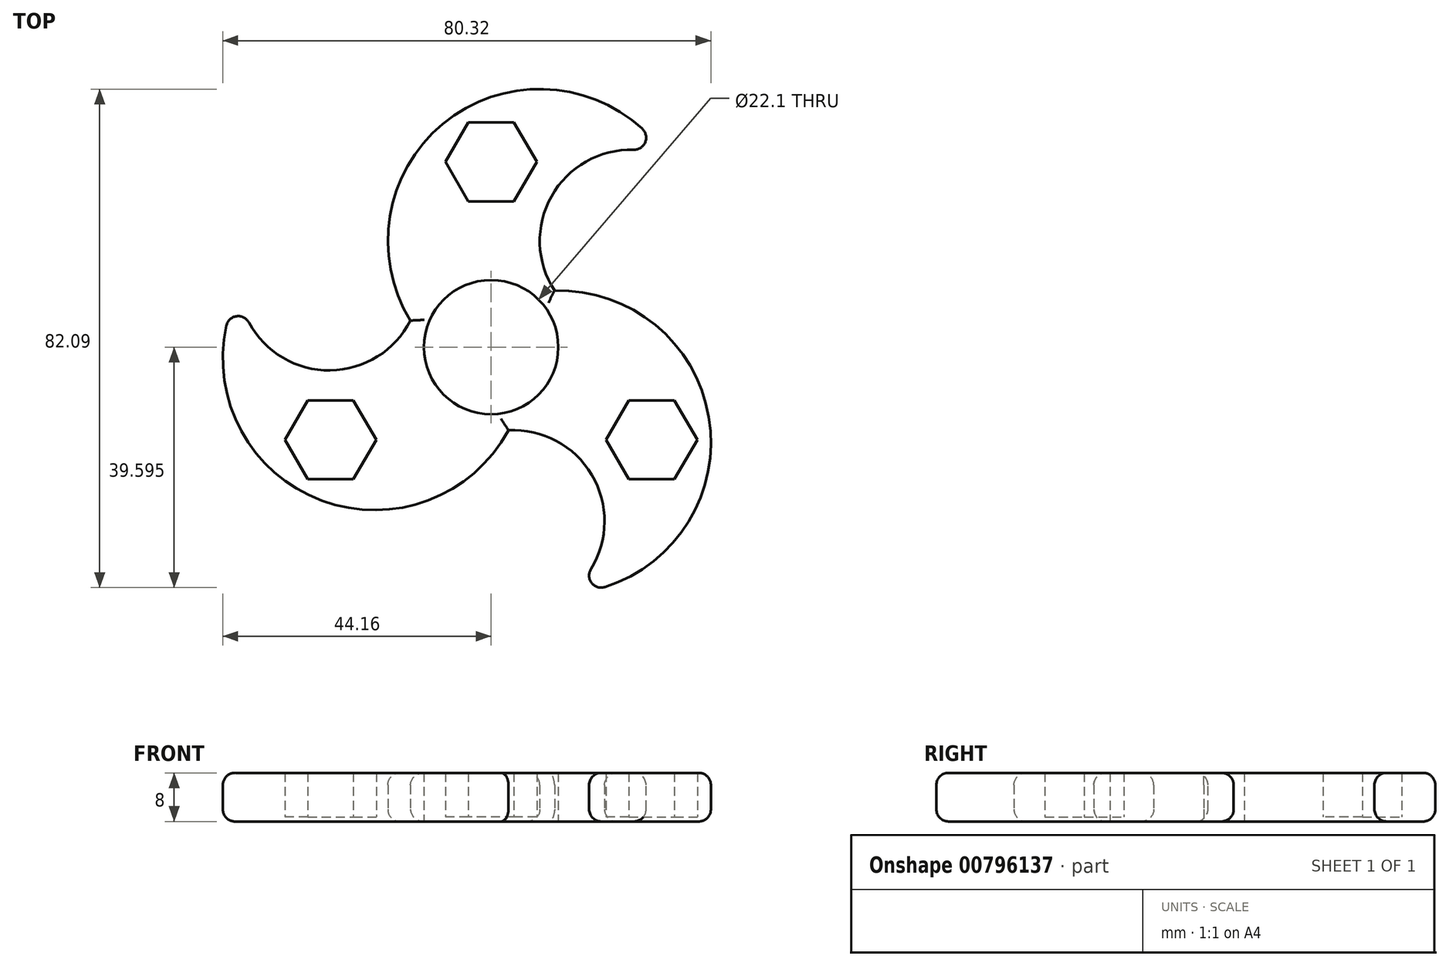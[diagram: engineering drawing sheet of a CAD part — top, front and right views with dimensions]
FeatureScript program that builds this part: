
annotation { "Feature Type Name" : "Feature", "Feature Type Description" : "" }
export const myFeature = defineFeature(function(context is Context, id is Id, definition is map)
    precondition{}
    {
        {
            var Q0;
            Q0=qCreatedBy(makeId("Top.planeOp"),FACE);
            var sketch = newSketch(context, id + "F0", { "sketchPlane" : qUnion([Q0])});
            skCircle(sketch, "E0", {"center": v(0, -1.85) * mm, "radius": 11.05 * mm});
            skLineSegment(sketch, "E1", {"start": v(0, -1.85) * mm, "end": v(0, 49.7) * mm, "construction": true});
            skLineSegment(sketch, "E2", {"start": v(0, -1.85) * mm, "end": v(-44.64, -27.62) * mm, "construction": true});
            skLineSegment(sketch, "E3", {"start": v(0, -1.85) * mm, "end": v(44.64, -27.62) * mm, "construction": true});
            skCircle(sketch, "E4", {"center": v(0, -1.85) * mm, "radius": 30.5 * mm, "construction": true});
            skPoint(sketch, "E5", {"position": v(-26.41, -17.1) * mm});
            skPoint(sketch, "E6", {"position": v(26.41, -17.1) * mm});
            skPoint(sketch, "E7", {"position": v(0, 28.65) * mm});
            skCircle(sketch, "E8", {"center": v(0, -1.85) * mm, "radius": 17.5 * mm, "construction": true});
            skPoint(sketch, "E9", {"position": v(0, 15.65) * mm});
            skPoint(sketch, "E10", {"position": v(15.16, -10.6) * mm});
            skPoint(sketch, "E11", {"position": v(-15.16, -10.6) * mm});
            skLineSegment(sketch, "E12", {"start": v(-15.16, -10.6) * mm, "end": v(-23.16, 3.26) * mm, "construction": true});
            skLineSegment(sketch, "E13", {"start": v(-15.16, -10.6) * mm, "end": v(-7.16, -24.45) * mm, "construction": true});
            skLineSegment(sketch, "E14", {"start": v(15.16, -10.6) * mm, "end": v(7.16, -24.45) * mm, "construction": true});
            skLineSegment(sketch, "E15", {"start": v(15.16, -10.6) * mm, "end": v(23.16, 3.26) * mm, "construction": true});
            skLineSegment(sketch, "E16", {"start": v(0, 15.65) * mm, "end": v(16, 15.65) * mm, "construction": true});
            skLineSegment(sketch, "E17", {"start": v(0, 15.65) * mm, "end": v(-16, 15.65) * mm, "construction": true});
            skPoint(sketch, "E18", {"position": v(-19.16, -3.67) * mm});
            skPoint(sketch, "E19", {"position": v(-11.16, -17.52) * mm});
            skPoint(sketch, "E20", {"position": v(-8, 15.65) * mm});
            skPoint(sketch, "E21", {"position": v(8, 15.65) * mm});
            skPoint(sketch, "E22", {"position": v(19.16, -3.67) * mm});
            skPoint(sketch, "E23", {"position": v(11.16, -17.52) * mm});
            skCircle(sketch, "E24", {"center": v(0, -1.85) * mm, "radius": 14 * mm});
            skCircle(sketch, "E25", {"center": v(8, 15.65) * mm, "radius": 25 * mm});
            skCircle(sketch, "E26", {"center": v(11.16, -17.52) * mm, "radius": 25 * mm});
            skCircle(sketch, "E27", {"center": v(-19.16, -3.67) * mm, "radius": 25 * mm});
            skCircle(sketch, "E28.cCircle", {"center": v(0, 28.65) * mm, "radius": 6.5 * mm, "construction": true});
            skLineSegment(sketch, "E28.0", {"start": v(3.75, 22.15) * mm, "end": v(-3.75, 22.15) * mm});
            skLineSegment(sketch, "E28.1", {"start": v(-3.75, 22.15) * mm, "end": v(-7.5, 28.65) * mm});
            skLineSegment(sketch, "E28.2", {"start": v(-7.5, 28.65) * mm, "end": v(-3.75, 35.15) * mm});
            skLineSegment(sketch, "E28.3", {"start": v(-3.75, 35.15) * mm, "end": v(3.75, 35.15) * mm});
            skLineSegment(sketch, "E28.4", {"start": v(3.75, 35.15) * mm, "end": v(7.5, 28.65) * mm});
            skLineSegment(sketch, "E28.5", {"start": v(7.5, 28.65) * mm, "end": v(3.75, 22.15) * mm});
            skPoint(sketch, "E28.0.midPoint", {"position": v(0, 22.15) * mm});
            skCircle(sketch, "E29.cCircle", {"center": v(26.41, -17.1) * mm, "radius": 6.5 * mm, "construction": true});
            skLineSegment(sketch, "E29.0", {"start": v(18.9, -17.1) * mm, "end": v(22.66, -10.6) * mm});
            skLineSegment(sketch, "E29.1", {"start": v(22.66, -10.6) * mm, "end": v(30.17, -10.6) * mm});
            skLineSegment(sketch, "E29.2", {"start": v(30.17, -10.6) * mm, "end": v(33.92, -17.1) * mm});
            skLineSegment(sketch, "E29.3", {"start": v(33.92, -17.1) * mm, "end": v(30.17, -23.6) * mm});
            skLineSegment(sketch, "E29.4", {"start": v(30.17, -23.6) * mm, "end": v(22.66, -23.6) * mm});
            skLineSegment(sketch, "E29.5", {"start": v(22.66, -23.6) * mm, "end": v(18.9, -17.1) * mm});
            skPoint(sketch, "E29.0.midPoint", {"position": v(20.78, -13.85) * mm});
            skCircle(sketch, "E30.cCircle", {"center": v(-26.41, -17.1) * mm, "radius": 6.5 * mm, "construction": true});
            skLineSegment(sketch, "E30.0", {"start": v(-22.66, -10.6) * mm, "end": v(-18.9, -17.1) * mm});
            skLineSegment(sketch, "E30.1", {"start": v(-18.9, -17.1) * mm, "end": v(-22.66, -23.6) * mm});
            skLineSegment(sketch, "E30.2", {"start": v(-22.66, -23.6) * mm, "end": v(-30.17, -23.6) * mm});
            skLineSegment(sketch, "E30.3", {"start": v(-30.17, -23.6) * mm, "end": v(-33.92, -17.1) * mm});
            skLineSegment(sketch, "E30.4", {"start": v(-33.92, -17.1) * mm, "end": v(-30.17, -10.6) * mm});
            skLineSegment(sketch, "E30.5", {"start": v(-30.17, -10.6) * mm, "end": v(-22.66, -10.6) * mm});
            skPoint(sketch, "E30.0.midPoint", {"position": v(-20.78, -13.85) * mm});
            skPoint(sketch, "E31", {"position": v(23, 15.65) * mm});
            skPoint(sketch, "E32", {"position": v(-26.66, 9.32) * mm});
            skPoint(sketch, "E33", {"position": v(3.66, -30.51) * mm});
            skCircle(sketch, "E34", {"center": v(23, 15.65) * mm, "radius": 15 * mm});
            skCircle(sketch, "E35", {"center": v(3.66, -30.51) * mm, "radius": 15 * mm});
            skCircle(sketch, "E36", {"center": v(-26.66, 9.32) * mm, "radius": 15 * mm});
            skSolve(sketch);
        }
        {
            var Q0;
            Q0=makeQuery(id+"F0.imprint","IMPRINT",FACE,{"disambiguationData":[TD([[makeQuery(id+"F0.imprint","IMPRINT",EDGE,{"derivedFrom":sQuery(id+"F0.wireOp",EDGE,"E30.0")}),1.0]])]});
            var Q1;
            Q1=makeQuery(id+"F0.imprint","IMPRINT",FACE,{"disambiguationData":[TD([[makeQuery(id+"F0.imprint","IMPRINT",EDGE,{"derivedFrom":sQuery(id+"F0.wireOp",EDGE,"E28.0")}),1.0]])]});
            var Q2;
            Q2=makeQuery(id+"F0.imprint","IMPRINT",FACE,{"disambiguationData":[TD([[makeQuery(id+"F0.imprint","IMPRINT",EDGE,{"derivedFrom":sQuery(id+"F0.wireOp",EDGE,"E29.0")}),1.0]])]});
            var Q3;
            {var subQ1=sQuery(id+"F0.wireOp",EDGE,"E0");var subQ5=sQuery(id+"F0.wireOp",EDGE,"E25");var subQ6=makeQuery(id+"F0.imprint","INTERSECT",VERTEX,{"disambiguationData":[OD(0.0)],"derivedFrom":[subQ1,subQ5]});Q3=makeQuery(id+"F0.imprint","IMPRINT",FACE,{"disambiguationData":[TD([[makeQuery(id+"F0.imprint","IMPRINT",EDGE,{"disambiguationData":[TD([[subQ6,-1.0]])],"derivedFrom":subQ1}),-1.0]])]});}
            var Q4;
            {var subQ0=sQuery(id+"F0.wireOp",EDGE,"E27");var subQ1=sQuery(id+"F0.wireOp",EDGE,"E0");var subQ2=makeQuery(id+"F0.imprint","INTERSECT",VERTEX,{"disambiguationData":[OD(0.0)],"derivedFrom":[subQ1,subQ0]});Q4=makeQuery(id+"F0.imprint","IMPRINT",FACE,{"disambiguationData":[TD([[makeQuery(id+"F0.imprint","IMPRINT",EDGE,{"disambiguationData":[TD([[subQ2,-1.0]])],"derivedFrom":subQ1}),-1.0]])]});}
            var Q5;
            {var subQ0=sQuery(id+"F0.wireOp",EDGE,"E27");var subQ1=sQuery(id+"F0.wireOp",EDGE,"E0");var subQ2=makeQuery(id+"F0.imprint","INTERSECT",VERTEX,{"disambiguationData":[OD(0.0)],"derivedFrom":[subQ1,subQ0]});Q5=makeQuery(id+"F0.imprint","IMPRINT",FACE,{"disambiguationData":[TD([[makeQuery(id+"F0.imprint","IMPRINT",EDGE,{"disambiguationData":[TD([[subQ2,1.0]])],"derivedFrom":subQ1}),-1.0]])]});}
            var Q6;
            {var subQ0=sQuery(id+"F0.wireOp",EDGE,"E26");var subQ1=sQuery(id+"F0.wireOp",EDGE,"E0");var subQ2=makeQuery(id+"F0.imprint","INTERSECT",VERTEX,{"disambiguationData":[OD(0.0)],"derivedFrom":[subQ1,subQ0]});Q6=makeQuery(id+"F0.imprint","IMPRINT",FACE,{"disambiguationData":[TD([[makeQuery(id+"F0.imprint","IMPRINT",EDGE,{"disambiguationData":[TD([[subQ2,1.0]])],"derivedFrom":subQ1}),-1.0]])]});}
            var Q7;
            {var subQ0=sQuery(id+"F0.wireOp",EDGE,"E27");var subQ1=sQuery(id+"F0.wireOp",EDGE,"E0");var subQ2=makeQuery(id+"F0.imprint","INTERSECT",VERTEX,{"disambiguationData":[OD(1.0)],"derivedFrom":[subQ1,subQ0]});Q7=makeQuery(id+"F0.imprint","IMPRINT",FACE,{"disambiguationData":[TD([[makeQuery(id+"F0.imprint","IMPRINT",EDGE,{"disambiguationData":[TD([[subQ2,-1.0]])],"derivedFrom":subQ1}),-1.0]])]});}
            var Q8;
            {var subQ1=sQuery(id+"F0.wireOp",EDGE,"E0");var subQ5=sQuery(id+"F0.wireOp",EDGE,"E26");var subQ6=makeQuery(id+"F0.imprint","INTERSECT",VERTEX,{"disambiguationData":[OD(1.0)],"derivedFrom":[subQ1,subQ5]});Q8=makeQuery(id+"F0.imprint","IMPRINT",FACE,{"disambiguationData":[TD([[makeQuery(id+"F0.imprint","IMPRINT",EDGE,{"disambiguationData":[TD([[subQ6,-1.0]])],"derivedFrom":subQ1}),-1.0]])]});}
            var Q9;
            {var subQ0=sQuery(id+"F0.wireOp",EDGE,"E36");var subQ1=sQuery(id+"F0.wireOp",EDGE,"E24");var subQ2=makeQuery(id+"F0.imprint","INTERSECT",VERTEX,{"disambiguationData":[OD(0.0)],"derivedFrom":[subQ1,subQ0]});Q9=makeQuery(id+"F0.imprint","IMPRINT",FACE,{"disambiguationData":[TD([[makeQuery(id+"F0.imprint","IMPRINT",EDGE,{"disambiguationData":[TD([[subQ2,-1.0]])],"derivedFrom":subQ1}),-1.0]])]});}
            var Q10;
            {var subQ0=sQuery(id+"F0.wireOp",EDGE,"E27");var subQ1=sQuery(id+"F0.wireOp",EDGE,"E24");var subQ2=makeQuery(id+"F0.imprint","INTERSECT",VERTEX,{"disambiguationData":[OD(0.0)],"derivedFrom":[subQ1,subQ0]});Q10=makeQuery(id+"F0.imprint","IMPRINT",FACE,{"disambiguationData":[TD([[makeQuery(id+"F0.imprint","IMPRINT",EDGE,{"disambiguationData":[TD([[subQ2,-1.0]])],"derivedFrom":subQ1}),-1.0]])]});}
            var Q11;
            {var subQ0=sQuery(id+"F0.wireOp",EDGE,"E26");var subQ1=sQuery(id+"F0.wireOp",EDGE,"E24");var subQ2=makeQuery(id+"F0.imprint","INTERSECT",VERTEX,{"disambiguationData":[OD(0.0)],"derivedFrom":[subQ1,subQ0]});Q11=makeQuery(id+"F0.imprint","IMPRINT",FACE,{"disambiguationData":[TD([[makeQuery(id+"F0.imprint","IMPRINT",EDGE,{"disambiguationData":[TD([[subQ2,1.0]])],"derivedFrom":subQ1}),-1.0]])]});}
            var Q12;
            {var subQ0=sQuery(id+"F0.wireOp",EDGE,"E34");var subQ1=sQuery(id+"F0.wireOp",EDGE,"E24");var subQ2=makeQuery(id+"F0.imprint","INTERSECT",VERTEX,{"disambiguationData":[OD(0.0)],"derivedFrom":[subQ1,subQ0]});Q12=makeQuery(id+"F0.imprint","IMPRINT",FACE,{"disambiguationData":[TD([[makeQuery(id+"F0.imprint","IMPRINT",EDGE,{"disambiguationData":[TD([[subQ2,1.0]])],"derivedFrom":subQ1}),-1.0]])]});}
            var Q13;
            {var subQ0=sQuery(id+"F0.wireOp",EDGE,"E26");var subQ1=sQuery(id+"F0.wireOp",EDGE,"E24");var subQ2=makeQuery(id+"F0.imprint","INTERSECT",VERTEX,{"disambiguationData":[OD(1.0)],"derivedFrom":[subQ1,subQ0]});Q13=makeQuery(id+"F0.imprint","IMPRINT",FACE,{"disambiguationData":[TD([[makeQuery(id+"F0.imprint","IMPRINT",EDGE,{"disambiguationData":[TD([[subQ2,-1.0]])],"derivedFrom":subQ1}),-1.0]])]});}
            var Q14;
            {var subQ0=sQuery(id+"F0.wireOp",EDGE,"E35");var subQ1=sQuery(id+"F0.wireOp",EDGE,"E24");var subQ2=makeQuery(id+"F0.imprint","INTERSECT",VERTEX,{"disambiguationData":[OD(0.0)],"derivedFrom":[subQ1,subQ0]});Q14=makeQuery(id+"F0.imprint","IMPRINT",FACE,{"disambiguationData":[TD([[makeQuery(id+"F0.imprint","IMPRINT",EDGE,{"disambiguationData":[TD([[subQ2,-1.0]])],"derivedFrom":subQ1}),-1.0]])]});}
            var Q15;
            {var subQ0=sQuery(id+"F0.wireOp",EDGE,"E36");var subQ1=sQuery(id+"F0.wireOp",EDGE,"E24");var subQ2=makeQuery(id+"F0.imprint","INTERSECT",VERTEX,{"disambiguationData":[OD(0.0)],"derivedFrom":[subQ1,subQ0]});Q15=makeQuery(id+"F0.imprint","IMPRINT",FACE,{"disambiguationData":[TD([[makeQuery(id+"F0.imprint","IMPRINT",EDGE,{"disambiguationData":[TD([[subQ2,-1.0]])],"derivedFrom":subQ1}),1.0]])]});}
            var Q16;
            {var subQ0=sQuery(id+"F0.wireOp",EDGE,"E26");var subQ1=sQuery(id+"F0.wireOp",EDGE,"E24");var subQ2=makeQuery(id+"F0.imprint","INTERSECT",VERTEX,{"disambiguationData":[OD(0.0)],"derivedFrom":[subQ1,subQ0]});Q16=makeQuery(id+"F0.imprint","IMPRINT",FACE,{"disambiguationData":[TD([[makeQuery(id+"F0.imprint","IMPRINT",EDGE,{"disambiguationData":[TD([[subQ2,1.0]])],"derivedFrom":subQ1}),1.0]])]});}
            var Q17;
            {var subQ0=sQuery(id+"F0.wireOp",EDGE,"E35");var subQ1=sQuery(id+"F0.wireOp",EDGE,"E24");var subQ2=makeQuery(id+"F0.imprint","INTERSECT",VERTEX,{"disambiguationData":[OD(0.0)],"derivedFrom":[subQ1,subQ0]});Q17=makeQuery(id+"F0.imprint","IMPRINT",FACE,{"disambiguationData":[TD([[makeQuery(id+"F0.imprint","IMPRINT",EDGE,{"disambiguationData":[TD([[subQ2,-1.0]])],"derivedFrom":subQ1}),1.0]])]});}
            extrude(context, id + "F1", {"entities" : qUnion([Q0, Q1, Q2, Q3, Q4, Q5, Q6, Q7, Q8, Q9, Q10, Q11, Q12, Q13, Q14, Q15, Q16, Q17]), "depth" : 8 * mm, "offsetDistance" : 25 * mm});
        }
        {
            var Q0;
            Q0=makeQuery(id+"F0.imprint","IMPRINT",FACE,{"disambiguationData":[TD([[makeQuery(id+"F0.imprint","IMPRINT",EDGE,{"derivedFrom":sQuery(id+"F0.wireOp",EDGE,"61c12435-9293-4a2a-be9d-d5ba2b4efff9.0")}),-1.0]])]});
            var Q1;
            Q1=makeQuery(id+"F0.imprint","IMPRINT",FACE,{"disambiguationData":[TD([[makeQuery(id+"F0.imprint","IMPRINT",EDGE,{"derivedFrom":sQuery(id+"F0.wireOp",EDGE,"E30.0")}),-1.0]])]});
            var Q2;
            Q2=makeQuery(id+"F0.imprint","IMPRINT",FACE,{"disambiguationData":[TD([[makeQuery(id+"F0.imprint","IMPRINT",EDGE,{"derivedFrom":sQuery(id+"F0.wireOp",EDGE,"0f203aee-2d51-47dd-945b-47dc9215cd85.0")}),-1.0]])]});
            var Q3;
            Q3=makeQuery(id+"F0.imprint","IMPRINT",FACE,{"disambiguationData":[TD([[makeQuery(id+"F0.imprint","IMPRINT",EDGE,{"derivedFrom":sQuery(id+"F0.wireOp",EDGE,"E29.0")}),-1.0]])]});
            var Q4;
            Q4=makeQuery(id+"F0.imprint","IMPRINT",FACE,{"disambiguationData":[TD([[makeQuery(id+"F0.imprint","IMPRINT",EDGE,{"derivedFrom":sQuery(id+"F0.wireOp",EDGE,"E28.0")}),-1.0]])]});
            var Q5;
            Q5=makeQuery(id+"F0.imprint","IMPRINT",FACE,{"disambiguationData":[TD([[makeQuery(id+"F0.imprint","IMPRINT",EDGE,{"derivedFrom":sQuery(id+"F0.wireOp",EDGE,"1ad6b149-f255-4b0b-b5b7-08b1ead0d9f5.0")}),-1.0]])]});
            extrude(context, id + "F2", {"entities" : qUnion([Q0, Q1, Q2, Q3, Q4, Q5]), "operationType" : NewBodyOperationType.ADD, "depth" : 0.75 * mm, "offsetDistance" : 25 * mm});
        }
        {
            var Q0;
            Q0=makeQuery(id+"F1.opExtrude","SWEPT_EDGE",EDGE,{"disambiguationData":[OSD([sQuery(id+"F0.wireOp",EDGE,"E25"),sQuery(id+"F0.wireOp",EDGE,"E34")])]});
            var Q1;
            Q1=makeQuery(id+"F1.opExtrude","SWEPT_EDGE",EDGE,{"disambiguationData":[OSD([sQuery(id+"F0.wireOp",EDGE,"E26"),sQuery(id+"F0.wireOp",EDGE,"E35")])]});
            var Q2;
            Q2=makeQuery(id+"F1.opExtrude","SWEPT_EDGE",EDGE,{"disambiguationData":[OSD([sQuery(id+"F0.wireOp",EDGE,"E27"),sQuery(id+"F0.wireOp",EDGE,"E36")])]});
            fillet(context, id + "F3", {"entities" : qUnion([Q0, Q1, Q2]), "radius" : 2 * mm, "tangentPropagation" : true, "allowEdgeOverflow" : false});
        }
        {
            var Q0;
            Q0=makeQuery(id+"F1.opExtrude","CAP_EDGE",EDGE,{"disambiguationData":[OSD([sQuery(id+"F0.wireOp",EDGE,"E25")])],"isStart":false});
            var Q1;
            Q1=makeQuery(id+"F1.opExtrude","CAP_EDGE",EDGE,{"disambiguationData":[OSD([sQuery(id+"F0.wireOp",EDGE,"E26")])],"isStart":false});
            var Q2;
            Q2=makeQuery(id+"F1.opExtrude","CAP_EDGE",EDGE,{"disambiguationData":[OSD([sQuery(id+"F0.wireOp",EDGE,"E27")])],"isStart":true});
            var Q3;
            Q3=makeQuery(id+"F1.opExtrude","CAP_EDGE",EDGE,{"disambiguationData":[OSD([sQuery(id+"F0.wireOp",EDGE,"E27")])],"isStart":false});
            var Q4;
            Q4=makeQuery(id+"F1.opExtrude","CAP_EDGE",EDGE,{"disambiguationData":[OSD([sQuery(id+"F0.wireOp",EDGE,"E25")])],"isStart":true});
            var Q5;
            Q5=makeQuery(id+"F1.opExtrude","CAP_EDGE",EDGE,{"disambiguationData":[OSD([sQuery(id+"F0.wireOp",EDGE,"E26")])],"isStart":true});
            fillet(context, id + "F4", {"entities" : qUnion([Q0, Q1, Q2, Q3, Q4, Q5]), "radius" : 2 * mm, "tangentPropagation" : true, "allowEdgeOverflow" : false});
        }
    });
